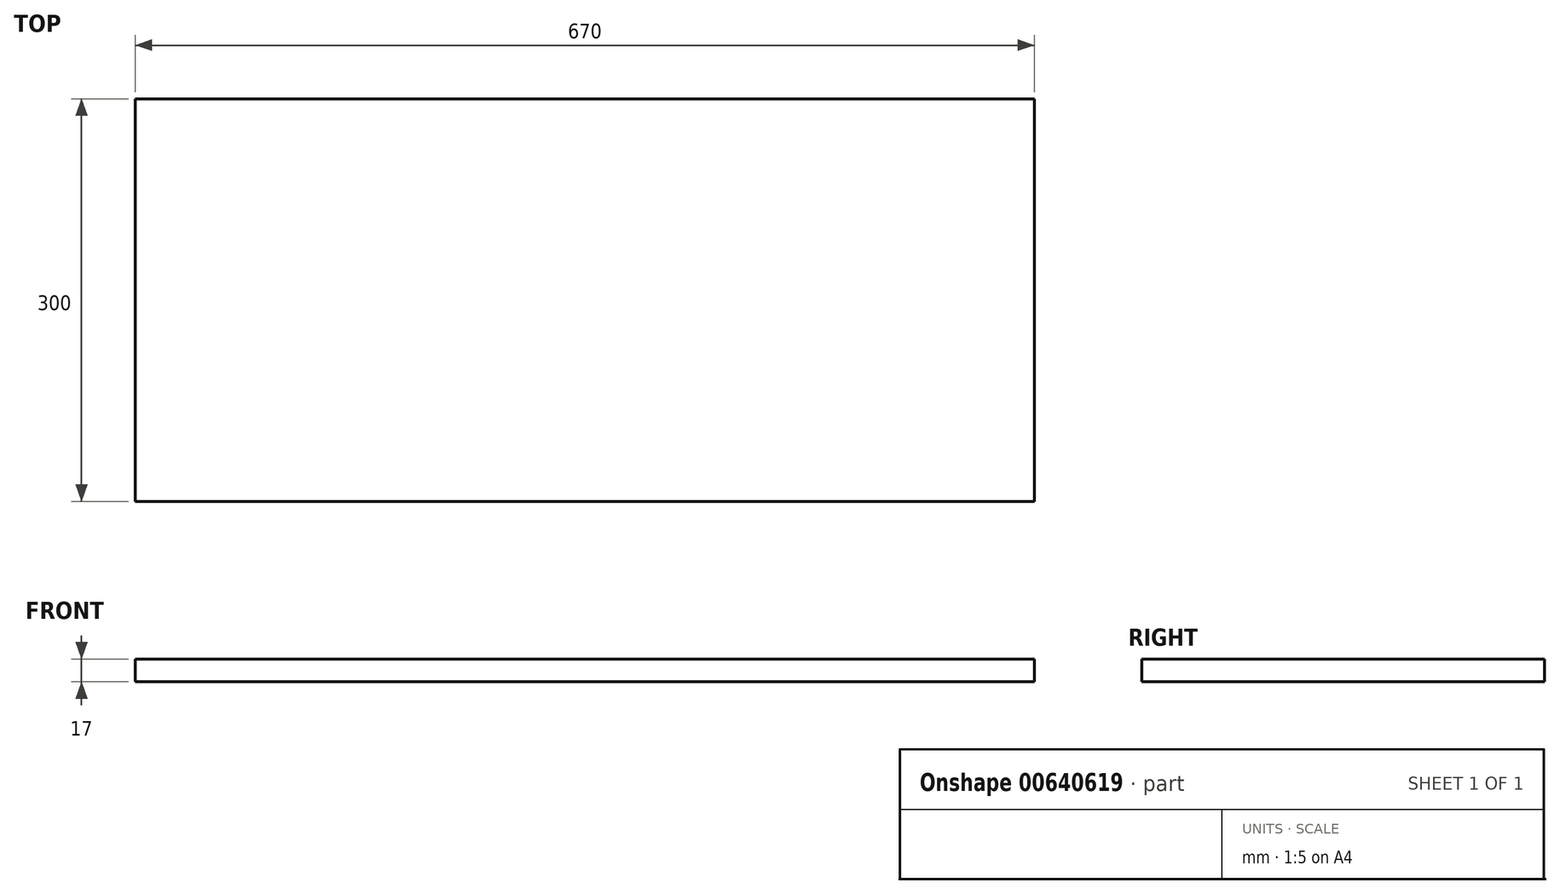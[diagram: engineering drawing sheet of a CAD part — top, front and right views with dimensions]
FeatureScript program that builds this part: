
annotation { "Feature Type Name" : "Feature", "Feature Type Description" : "" }
export const myFeature = defineFeature(function(context is Context, id is Id, definition is map)
    precondition{}
    {
        {
            var Q0;
            Q0=qCreatedBy(makeId("Top.planeOp"),FACE);
            var sketch = newSketch(context, id + "F0", { "sketchPlane" : qUnion([Q0])});
            skLineSegment(sketch, "E0.bottom", {"start": v(0, 0) * mm, "end": v(670, 0) * mm});
            skLineSegment(sketch, "E0.top", {"start": v(0, 300) * mm, "end": v(670, 300) * mm});
            skLineSegment(sketch, "E0.left", {"start": v(0, 0) * mm, "end": v(0, 300) * mm});
            skLineSegment(sketch, "E0.right", {"start": v(670, 0) * mm, "end": v(670, 300) * mm});
            skSolve(sketch);
        }
        {
            var Q0;
            Q0 = qSketchRegion(id + "F0", true);
            extrude(context, id + "F1", {"entities" : qUnion([Q0]), "depth" : 17 * mm, "offsetDistance" : 25 * mm});
        }
    });
